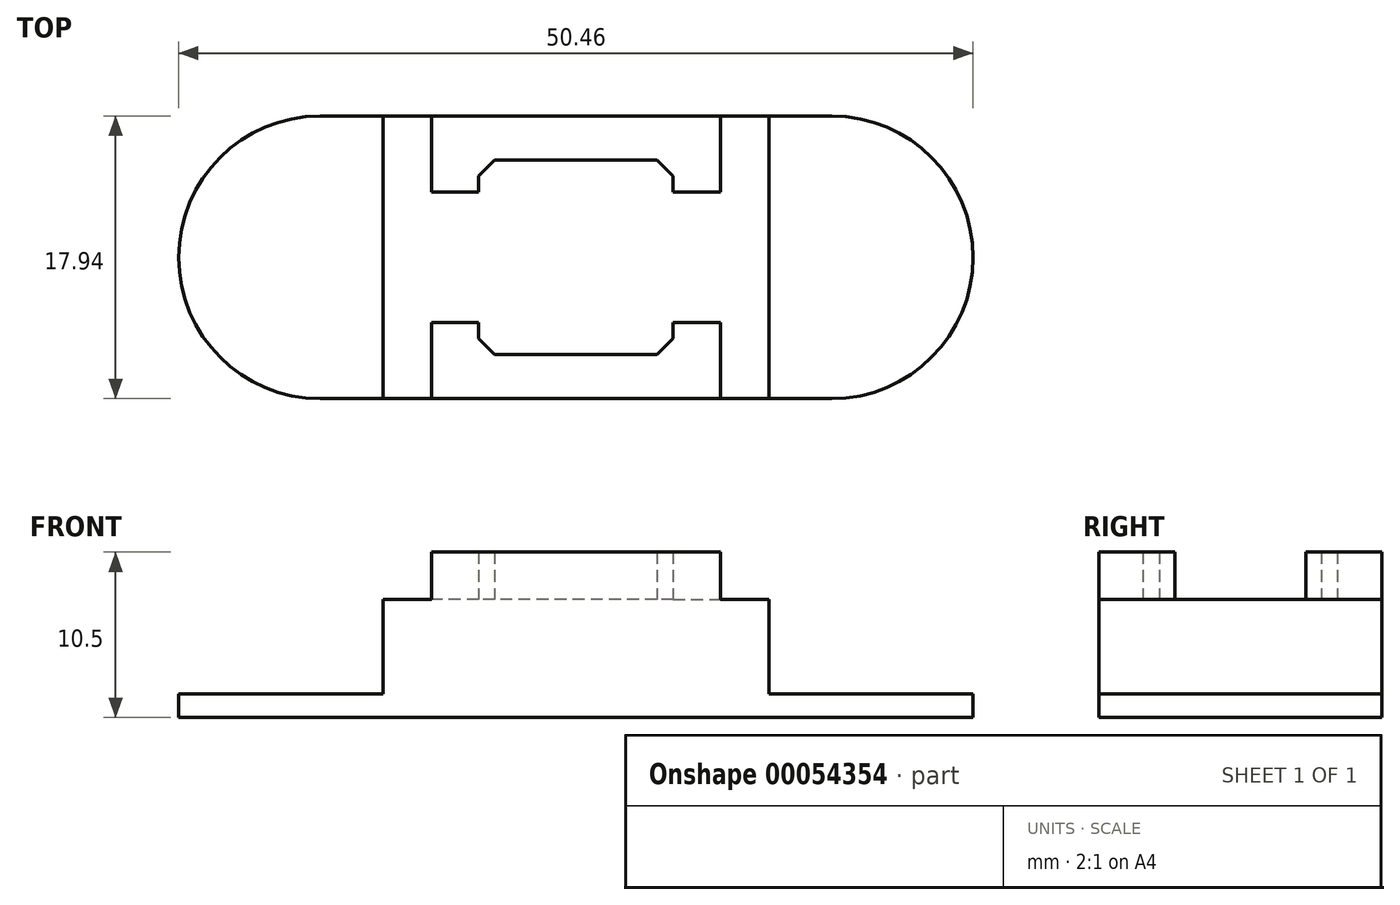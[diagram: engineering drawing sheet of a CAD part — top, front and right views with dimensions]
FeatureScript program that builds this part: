
annotation { "Feature Type Name" : "Feature", "Feature Type Description" : "" }
export const myFeature = defineFeature(function(context is Context, id is Id, definition is map)
    precondition{}
    {
        {
            var Q0;
            Q0=qCreatedBy(makeId("Top.planeOp"),FACE);
            var sketch = newSketch(context, id + "F0", { "sketchPlane" : qUnion([Q0])});
            skLineSegment(sketch, "E0", {"start": v(0, 0) * mm, "end": v(-16.25, 0) * mm});
            skLineSegment(sketch, "E1", {"start": v(0, 0) * mm, "end": v(16.25, 0) * mm});
            skLineSegment(sketch, "E2", {"start": v(-16.25, 0) * mm, "end": v(-16.25, 8.97) * mm});
            skLineSegment(sketch, "E3", {"start": v(-16.25, 0) * mm, "end": v(-16.25, -8.98) * mm});
            skLineSegment(sketch, "E4", {"start": v(16.25, 0) * mm, "end": v(16.25, 8.97) * mm});
            skLineSegment(sketch, "E5", {"start": v(16.25, 0) * mm, "end": v(16.25, -8.97) * mm});
            skLineSegment(sketch, "E6", {"start": v(-16.25, 8.97) * mm, "end": v(16.25, 8.97) * mm});
            skLineSegment(sketch, "E7", {"start": v(-16.25, -8.97) * mm, "end": v(16.25, -8.97) * mm});
            skArc(sketch, "E8", {"start": v(16.25, -8.97) * mm, "mid": v(25.23, 0) * mm, "end": v(16.25, 8.97) * mm});
            skArc(sketch, "E9", {"start": v(-16.25, 8.97) * mm, "mid": v(-25.22, 0) * mm, "end": v(-16.25, -8.98) * mm});
            skSolve(sketch);
        }
        {
            var Q0;
            Q0 = qSketchRegion(id + "F0", true);
            extrude(context, id + "F1", {"entities" : qUnion([Q0]), "depth" : 1.5 * mm});
        }
        {
            var Q0;
            Q0=makeQuery(id+"F1.opExtrude","CAP_FACE",FACE,{"disambiguationData":[OSD([sQuery(id+"F0.wireOp",EDGE,"E6"),sQuery(id+"F0.wireOp",EDGE,"E7"),sQuery(id+"F0.wireOp",EDGE,"E8"),sQuery(id+"F0.wireOp",EDGE,"E9")])],"isStart":false});
            var sketch = newSketch(context, id + "F2", { "sketchPlane" : qUnion([Q0])});
            skLineSegment(sketch, "E10", {"start": v(0, -1) * mm, "end": v(0, -8.97) * mm});
            skLineSegment(sketch, "E11", {"start": v(0, -1) * mm, "end": v(0, 8.97) * mm});
            skLineSegment(sketch, "E12", {"start": v(0, 8.97) * mm, "end": v(12.25, 8.98) * mm});
            skLineSegment(sketch, "E13", {"start": v(0, 8.97) * mm, "end": v(-12.25, 8.97) * mm});
            skLineSegment(sketch, "E14", {"start": v(0, -8.97) * mm, "end": v(-12.25, -8.97) * mm});
            skLineSegment(sketch, "E15", {"start": v(0, -8.97) * mm, "end": v(12.25, -8.97) * mm});
            skLineSegment(sketch, "E16", {"start": v(-12.25, 8.97) * mm, "end": v(-12.25, -8.97) * mm});
            skLineSegment(sketch, "E17", {"start": v(12.25, 8.97) * mm, "end": v(12.25, -8.97) * mm});
            skSolve(sketch);
        }
        {
            var Q0;
            Q0 = qSketchRegion(id + "F2", true);
            extrude(context, id + "F3", {"entities" : qUnion([Q0]), "operationType" : NewBodyOperationType.ADD, "depth" : 6 * mm});
        }
        {
            var Q0;
            Q0=makeQuery(id+"F3.opExtrude","CAP_FACE",FACE,{"disambiguationData":[OSD([sQuery(id+"F2.wireOp",EDGE,"E12"),sQuery(id+"F2.wireOp",EDGE,"E13"),sQuery(id+"F2.wireOp",EDGE,"E14"),sQuery(id+"F2.wireOp",EDGE,"E15"),sQuery(id+"F2.wireOp",EDGE,"E16"),sQuery(id+"F2.wireOp",EDGE,"E17")])],"isStart":false});
            var sketch = newSketch(context, id + "F4", { "sketchPlane" : qUnion([Q0])});
            skLineSegment(sketch, "E18", {"start": v(0, 0) * mm, "end": v(0, 6.17) * mm});
            skLineSegment(sketch, "E19", {"start": v(0, 6.17) * mm, "end": v(5.15, 6.17) * mm});
            skLineSegment(sketch, "E20", {"start": v(0, 0) * mm, "end": v(0, -6.18) * mm});
            skLineSegment(sketch, "E21", {"start": v(0, 0) * mm, "end": v(-6.17, 0) * mm});
            skLineSegment(sketch, "E22", {"start": v(0, -6.18) * mm, "end": v(5.15, -6.18) * mm});
            skLineSegment(sketch, "E23", {"start": v(0, -6.18) * mm, "end": v(-5.15, -6.18) * mm});
            skLineSegment(sketch, "E24", {"start": v(-6.17, 0) * mm, "end": v(-6.17, -5.15) * mm});
            skLineSegment(sketch, "E25", {"start": v(-6.17, 0) * mm, "end": v(-6.17, 5.15) * mm});
            skLineSegment(sketch, "E26", {"start": v(0, 6.17) * mm, "end": v(-5.15, 6.17) * mm});
            skLineSegment(sketch, "E27", {"start": v(-5.15, 6.17) * mm, "end": v(-6.18, 5.15) * mm});
            skLineSegment(sketch, "E28", {"start": v(-6.18, -5.15) * mm, "end": v(-5.15, -6.18) * mm});
            skLineSegment(sketch, "E29", {"start": v(0, 0) * mm, "end": v(6.18, 0) * mm});
            skLineSegment(sketch, "E30", {"start": v(6.17, 0) * mm, "end": v(6.17, 5.15) * mm});
            skLineSegment(sketch, "E31", {"start": v(6.18, 0) * mm, "end": v(6.18, -5.15) * mm});
            skLineSegment(sketch, "E32", {"start": v(6.17, 5.15) * mm, "end": v(5.15, 6.17) * mm});
            skLineSegment(sketch, "E33", {"start": v(6.18, -5.15) * mm, "end": v(5.15, -6.17) * mm});
            skLineSegment(sketch, "E34", {"start": v(-6.18, 5.15) * mm, "end": v(-6.18, 4.15) * mm});
            skLineSegment(sketch, "E35", {"start": v(-6.18, 4.15) * mm, "end": v(-9.18, 4.15) * mm});
            skLineSegment(sketch, "E36", {"start": v(-9.18, 4.15) * mm, "end": v(-9.18, 8.97) * mm});
            skLineSegment(sketch, "E37", {"start": v(6.17, 5.15) * mm, "end": v(6.17, 4.15) * mm});
            skLineSegment(sketch, "E38", {"start": v(6.17, 4.15) * mm, "end": v(9.17, 4.15) * mm});
            skLineSegment(sketch, "E39", {"start": v(9.17, 4.15) * mm, "end": v(9.17, 8.97) * mm});
            skLineSegment(sketch, "E40", {"start": v(9.17, 8.97) * mm, "end": v(-9.18, 8.97) * mm});
            skLineSegment(sketch, "E41", {"start": v(-6.17, -5.15) * mm, "end": v(-6.17, -4.15) * mm});
            skLineSegment(sketch, "E42", {"start": v(-6.18, -4.15) * mm, "end": v(-9.18, -4.15) * mm});
            skLineSegment(sketch, "E43", {"start": v(-9.17, -4.15) * mm, "end": v(-9.17, -8.98) * mm});
            skLineSegment(sketch, "E44", {"start": v(6.18, -5.15) * mm, "end": v(6.18, -4.15) * mm});
            skLineSegment(sketch, "E45", {"start": v(6.18, -4.15) * mm, "end": v(9.18, -4.15) * mm});
            skLineSegment(sketch, "E46", {"start": v(9.18, -4.15) * mm, "end": v(9.18, -8.97) * mm});
            skLineSegment(sketch, "E47", {"start": v(9.18, -8.97) * mm, "end": v(-9.17, -8.97) * mm});
            skSolve(sketch);
        }
        {
            var Q0;
            Q0=makeQuery(id+"F4.imprint","IMPRINT",FACE,{"disambiguationData":[TD([[makeQuery(id+"F4.imprint","IMPRINT",EDGE,{"derivedFrom":sQuery(id+"F4.wireOp",EDGE,"E22")}),-1.0]])]});
            var Q1;
            Q1=makeQuery(id+"F4.imprint","IMPRINT",FACE,{"disambiguationData":[TD([[makeQuery(id+"F4.imprint","IMPRINT",EDGE,{"derivedFrom":sQuery(id+"F4.wireOp",EDGE,"E19")}),1.0]])]});
            extrude(context, id + "F5", {"entities" : qUnion([Q0, Q1]), "operationType" : NewBodyOperationType.ADD, "depth" : 3 * mm});
        }
    });
